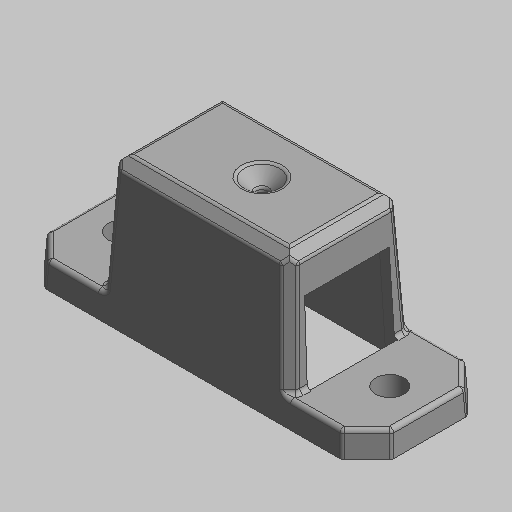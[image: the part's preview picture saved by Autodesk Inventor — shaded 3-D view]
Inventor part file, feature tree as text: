
AUTODESK INVENTOR PART (.ipt)
format: ipt  version: 2023.5 (Build 275446000, 446)  size: 629,248 bytes
history: native  units: mm (DEFAULTED — no unit token found)
features: fillet x1
ambient origin geometry x8: Origin, YZ Plane, XZ Plane, XY Plane, X Axis, Y Axis, Z Axis, Center Point
bodies: Solid1 (feature_tree)
feature tree (1):
  fillet  "Fillet5"  [1 undecoded]
note: 1 required parameter value undecoded (feature->parameter linkage not recoverable at this tier; creation-order binding heuristic only, values carry confidence <= 0.55)
